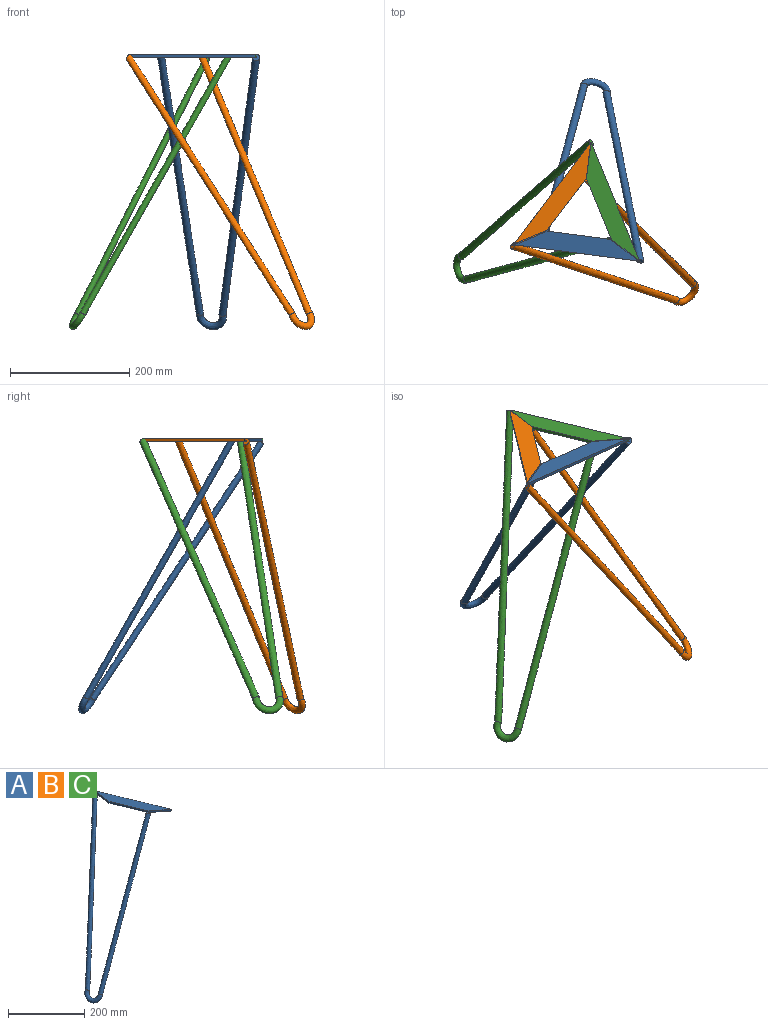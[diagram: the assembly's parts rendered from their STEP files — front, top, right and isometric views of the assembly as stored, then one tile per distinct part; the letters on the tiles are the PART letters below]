
ASSEMBLY  parts=3 mates=1
PART A: 11 faces, bbox 316x243.4x464.3 mm
  f0: plane 14.6x13.8mm, normal (0,0,1), area 66mm2, adj f4,f7,f8
  f1: plane 11.05x10.61mm, normal (0.8,0.39,0.47), area 98.2mm2, adj f2,f5,f6
  f2: bspline ~443.83x226.03mm, area 18157mm2, adj f1,f3,f5,f6,f10
  f3: bspline ~51.14x32.78mm, area 2432.1mm2, adj f2,f4
  f4: bspline ~431.55x256.45mm, area 17439.5mm2, adj f0,f3,f10
  f5: plane 59.55x8.12mm, normal (-0.99,0.13,0), area 285.6mm2, adj f1,f2,f6,f7,f9,f10
  f6: plane 200.31x82.18mm, normal (0.93,0.38,0), area 1080.4mm2, adj f1,f2,f5,f8,f9,f10
  f7: plane 104.16x42.73mm, normal (-0.93,-0.38,0), area 562.9mm2, adj f0,f5,f8,f9,f10
  f8: plane 47.48x36.69mm, normal (-0.61,-0.79,0), area 300mm2, adj f0,f6,f7,f9,f10
  f9: plane 200.31x90.21mm, normal (0,0,1), area 4936.3mm2, adj f5,f6,f7,f8
  f10: plane 196.05x91.55mm, normal (0,0,-1), area 4878.8mm2, adj f2,f4,f5,f6,f7,f8
PART B: same geometry as A
PART C: same geometry as A
PLACE A rot(axis=(0,0,-1),119.8deg) t=(-221,129.86,0)mm
PLACE B rot(axis=(0,0,1),120.6deg) t=(-220.16,128.65,0)mm
PLACE C t=(-220.84,128.74,0)mm
MATE revolute B.f9 <-> C.f9  axis (0,0,1) through (-212.13,193.16,5)mm
